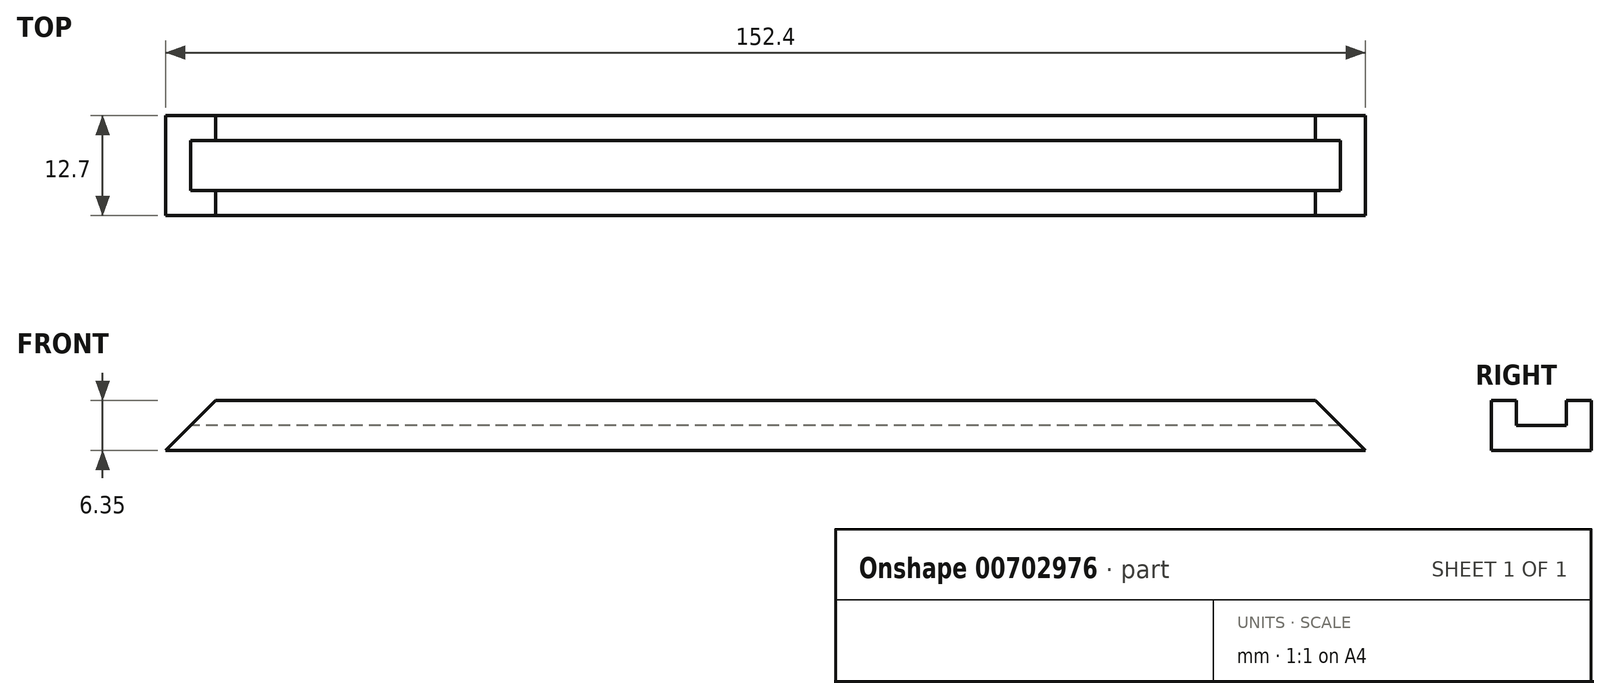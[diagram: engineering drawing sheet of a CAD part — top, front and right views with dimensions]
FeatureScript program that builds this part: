
annotation { "Feature Type Name" : "Feature", "Feature Type Description" : "" }
export const myFeature = defineFeature(function(context is Context, id is Id, definition is map)
    precondition{}
    {
        {
            var Q0;
            Q0=qCreatedBy(makeId("Right.planeOp"),FACE);
            var sketch = newSketch(context, id + "F0", { "sketchPlane" : qUnion([Q0])});
            skLineSegment(sketch, "E0.bottom", {"start": v(6.35, 3.18) * mm, "end": v(3.18, 3.18) * mm});
            skLineSegment(sketch, "E0.top", {"start": v(6.35, -3.18) * mm, "end": v(-6.35, -3.18) * mm});
            skLineSegment(sketch, "E0.left", {"start": v(6.35, 3.17) * mm, "end": v(6.35, -3.18) * mm});
            skLineSegment(sketch, "E0.right", {"start": v(-6.35, 3.17) * mm, "end": v(-6.35, -3.18) * mm});
            skPoint(sketch, "E0.middle", {"position": v(0, 0) * mm});
            skLineSegment(sketch, "E1.bottom", {"start": v(3.18, 0) * mm, "end": v(-3.17, 0) * mm});
            skLineSegment(sketch, "E1.left", {"start": v(3.18, 0) * mm, "end": v(3.18, 3.17) * mm});
            skLineSegment(sketch, "E1.right", {"start": v(-3.18, 0) * mm, "end": v(-3.18, 3.17) * mm});
            skPoint(sketch, "E1.middle", {"position": v(0, 3.18) * mm});
            skPoint(sketch, "E1.top.end.orphan", {"position": v(-3.18, 6.35) * mm});
            skPoint(sketch, "E1.top.start.orphan", {"position": v(3.18, 6.35) * mm});
            skLineSegment(sketch, "E2.trimOffspring", {"start": v(-3.18, 3.18) * mm, "end": v(-6.35, 3.18) * mm});
            skSolve(sketch);
        }
        {
            var Q0;
            Q0 = qSketchRegion(id + "F0", true);
            extrude(context, id + "F1", {"entities" : qUnion([Q0]), "depth" : 152.4 * mm, "offsetDistance" : 25.4 * mm});
        }
        {
            var Q0;
            Q0=qCreatedBy(makeId("Front.planeOp"),FACE);
            var sketch = newSketch(context, id + "F2", { "sketchPlane" : qUnion([Q0])});
            skLineSegment(sketch, "E3", {"start": v(0, -3.18) * mm, "end": v(6.35, 3.18) * mm});
            skLineSegment(sketch, "E4", {"start": v(6.35, 3.17) * mm, "end": v(0, 3.17) * mm});
            skLineSegment(sketch, "E5", {"start": v(0, 3.17) * mm, "end": v(0, -3.18) * mm});
            skLineSegment(sketch, "E6", {"start": v(152.4, -3.18) * mm, "end": v(152.4, 3.17) * mm});
            skLineSegment(sketch, "E7", {"start": v(152.4, 3.17) * mm, "end": v(146.05, 3.17) * mm});
            skLineSegment(sketch, "E8", {"start": v(146.05, 3.17) * mm, "end": v(152.4, -3.18) * mm});
            skSolve(sketch);
        }
        {
            var Q0;
            Q0 = qSketchRegion(id + "F2", true);
            extrude(context, id + "F3", {"entities" : qUnion([Q0]), "operationType" : NewBodyOperationType.REMOVE, "endBound" : BoundingType.SYMMETRIC, "oppositeDirection" : true, "depth" : 12.7 * mm, "offsetDistance" : 25.4 * mm});
        }
    });
